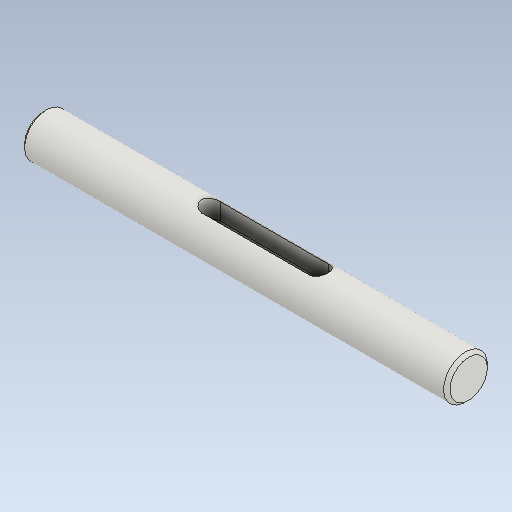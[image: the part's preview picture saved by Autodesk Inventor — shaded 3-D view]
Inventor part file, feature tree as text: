
AUTODESK INVENTOR PART (.ipt)
format: ipt  version: 2021 (Build 250183000, 183)  size: 130,048 bytes
history: native  units: mm
features: other x6, chamfer x2, revolve x1
ambient origin geometry x6: Origin, XZ Plane, XY Plane, X Axis, Y Axis, Z Axis
bodies: Body1 (feature_tree)
feature tree (9):
  other  "Твердое тело1"
  revolve  "Вращение1"
  other  "Шпоночный паз1"
  chamfer  "Фаска3"  [1 undecoded]
  chamfer  "Фаска2"  Distance=6.9mm
  other  "Начальная плоскость"
  other  "Исходная точка"
  other  "Основной эскиз"
  other  "iFeature11:1"
note: 1 required parameter value undecoded (feature->parameter linkage not recoverable at this tier; creation-order binding heuristic only, values carry confidence <= 0.55)
